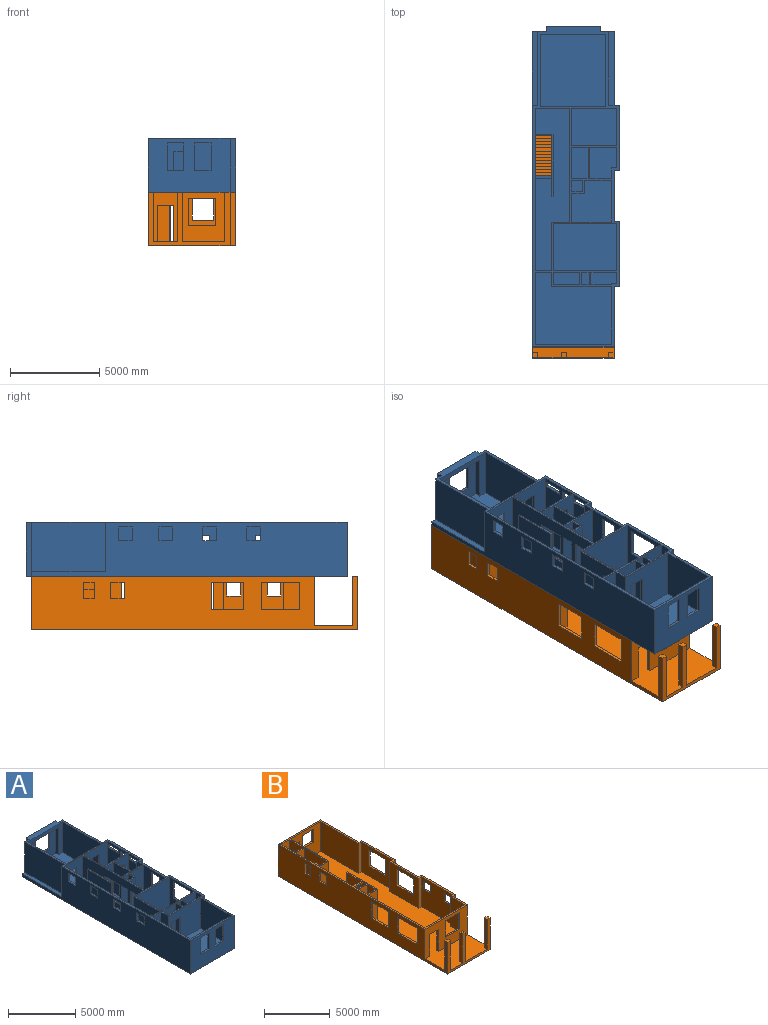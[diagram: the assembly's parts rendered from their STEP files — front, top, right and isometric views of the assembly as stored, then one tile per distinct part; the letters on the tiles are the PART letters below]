
ASSEMBLY  parts=2 mates=1
PART A: 174 faces, bbox 4876.8x17983.2x3025.8 mm
  f0: plane 17678.4x4572mm, normal (0,0,1), area 68948053.5mm2, adj f3,f4,f5,f7,f9,f10,f13,f15
  f1: plane 17983.2x4876.8mm, normal (0,0,-1), area 81833672.9mm2, adj f5,f6,f8,f11,f12,f14,f23,f24
  f2: plane 2565.4x101.6mm, normal (0,0,1), area 260644.6mm2, adj f4,f166,f167,f168
  f3: plane 1247.78x101.6mm, normal (0,-1,0), area 126773.9mm2, adj f0,f4,f166,f169
  f4: plane 3479.8x2771.78mm, normal (1,0,0), area 8251677mm2, adj f0,f2,f3,f167,f168,f169
  f5: plane 9118.6x3025.78mm, normal (1,0,0), area 23555975.7mm2, adj f0,f1,f49,f50,f58,f150,f151,f152
  f6: plane 17678.4x3025.78mm, normal (-1,0,0), area 39692581.9mm2, adj f1,f14,f22,f33,f36,f50,f150,f151
  f7: plane 2771.78x1143mm, normal (-1,0,0), area 2842978.2mm2, adj f0,f43,f50,f52,f141,f142,f143,f144
  f8: plane 3657.6x3025.78mm, normal (1,0,0), area 9371594.2mm2, adj f1,f26,f27,f50,f133,f134,f135,f136
  f9: plane 2771.78x2108.2mm, normal (-1,0,0), area 4473136.2mm2, adj f0,f42,f50,f53,f133,f134,f135,f136
  f10: plane 2771.78x2336.8mm, normal (-1,0,0), area 5362247.3mm2, adj f0,f50,f66,f78,f129,f130,f131,f132
  f11: plane 3025.78x2832.1mm, normal (1,0,0), area 7454460.9mm2, adj f1,f25,f26,f50,f129,f130,f131,f132
  f12: plane 3657.6x3025.78mm, normal (1,0,0), area 8279983.4mm2, adj f1,f24,f25,f50,f125,f126,f127,f128
  f13: plane 2771.78x2628.9mm, normal (-1,0,0), area 4499628.1mm2, adj f0,f16,f45,f50,f125,f126,f127,f128
  f14: plane 4572x3025.78mm, normal (0,-1,0), area 11046752.1mm2, adj f1,f6,f23,f50,f117,f118,f119,f120
  f15: plane 4267.2x2771.78mm, normal (0,1,0), area 9040627.1mm2, adj f0,f20,f48,f50,f117,f118,f119,f120
  f16: plane 3556x2771.78mm, normal (0,1,0), area 7946758.3mm2, adj f0,f13,f50,f65,f111,f112,f113
  f17: plane 3657.6x2771.78mm, normal (0,1,0), area 7144501.8mm2, adj f0,f18,f41,f50,f89,f90,f91,f92
  f18: plane 4038.6x2771.78mm, normal (1,0,0), area 11194090.5mm2, adj f0,f17,f37,f50
  f19: plane 2771.78x622.3mm, normal (-1,0,0), area 1724875.6mm2, adj f0,f46,f50,f64
  f20: plane 3238.5x2771.78mm, normal (-1,0,0), area 8976393.3mm2, adj f0,f15,f50,f61
  f21: plane 4140.2x304.8mm, normal (0,0,1), area 1261933mm2, adj f27,f28,f29,f34
  f22: plane 4140.2x304.8mm, normal (0,0,1), area 1261933mm2, adj f6,f33,f35,f36
  f23: plane 3390.9x3025.78mm, normal (1,0,0), area 10260100.4mm2, adj f1,f14,f24,f50
  f24: plane 3025.78x304.8mm, normal (0,-1,0), area 922256.2mm2, adj f1,f12,f23,f50
  f25: plane 3025.78x304.8mm, normal (0,1,0), area 922256.2mm2, adj f1,f11,f12,f50
  f26: plane 3025.78x304.8mm, normal (0,-1,0), area 922256.2mm2, adj f1,f8,f11,f50
  f27: plane 3025.78x609.6mm, normal (0,1,0), area 1767093.2mm2, adj f1,f8,f21,f28,f34,f50
  f28: plane 4140.2x254mm, normal (1,0,0), area 1051610.8mm2, adj f1,f21,f27,f29
  f29: plane 3025.78x762mm, normal (0,1,0), area 1460803.5mm2, adj f1,f21,f28,f30,f34,f50
  f30: plane 3025.78x304.8mm, normal (1,0,0), area 922256.2mm2, adj f1,f29,f31,f50
  f31: plane 3048x3025.78mm, normal (0,1,0), area 6899986.2mm2, adj f1,f30,f32,f50,f145,f146,f147,f148
  f32: plane 3025.78x304.8mm, normal (-1,0,0), area 922256.2mm2, adj f1,f31,f33,f50
  f33: plane 3025.78x762mm, normal (0,1,0), area 1460803.5mm2, adj f1,f6,f22,f32,f35,f50
  f34: plane 4140.2x2771.78mm, normal (1,0,0), area 11475702.9mm2, adj f21,f27,f29,f50
  f35: plane 4140.2x2771.78mm, normal (-1,0,0), area 11475702.9mm2, adj f22,f33,f36,f50
  f36: plane 2771.78x304.8mm, normal (0,1,0), area 844837mm2, adj f6,f22,f35,f50
  f37: plane 3657.6x2771.78mm, normal (0,-1,0), area 3370638.4mm2, adj f0,f18,f38,f40,f41,f50,f149
  f38: plane 2466.98x304.8mm, normal (1,0,0), area 751934mm2, adj f0,f37,f39,f149
  f39: plane 2743.2x2466.98mm, normal (0,-1,0), area 4444829.8mm2, adj f0,f38,f40,f145,f146,f147,f148,f149
  f40: plane 2466.98x304.8mm, normal (-1,0,0), area 751934mm2, adj f0,f37,f39,f149
  f41: plane 4038.6x2771.78mm, normal (-1,0,0), area 11194090.5mm2, adj f0,f17,f37,f50
  f42: plane 2771.78x2527.3mm, normal (0,-1,0), area 5559948.6mm2, adj f0,f9,f50,f54,f92,f93,f94
  f43: plane 2771.78x304.8mm, normal (0,1,0), area 844837mm2, adj f0,f7,f44,f50
  f44: plane 2771.78x596.9mm, normal (-1,0,0), area 1654472.5mm2, adj f0,f43,f50,f79
  f45: plane 3556x2771.78mm, normal (0,-1,0), area 9856431.9mm2, adj f0,f13,f50,f65
  f46: plane 2771.78x304.8mm, normal (0,1,0), area 844837mm2, adj f0,f19,f47,f50
  f47: plane 2771.78x50.8mm, normal (-1,0,0), area 140806.2mm2, adj f0,f46,f50,f62
  f48: plane 4013.2x2771.78mm, normal (1,0,0), area 11123687.4mm2, adj f0,f15,f50,f59
  f49: plane 2771.78x1943.1mm, normal (0,-1,0), area 3837452mm2, adj f0,f5,f50,f55,f89,f90,f91
  f50: plane 17983.2x4876.8mm, normal (0,0,1), area 11236106.6mm2, adj f5,f6,f7,f8,f9,f10,f11,f12
  f51: plane 2771.78x1739.9mm, normal (1,0,0), area 4822611.3mm2, adj f0,f50,f52,f79
  f52: plane 2771.78x1511.3mm, normal (0,-1,0), area 2743825.2mm2, adj f0,f7,f50,f51,f95,f96,f97
  f53: plane 2771.78x2527.3mm, normal (0,1,0), area 5559948.6mm2, adj f0,f9,f50,f54,f95,f96,f97
  f54: plane 2771.78x2108.2mm, normal (1,0,0), area 5843456.1mm2, adj f0,f42,f50,f53
  f55: plane 6388.1x2771.78mm, normal (-1,0,0), area 11925742.3mm2, adj f0,f49,f50,f56,f76,f82,f98,f99
  f56: plane 2771.78x1028.7mm, normal (0,1,0), area 2851324.9mm2, adj f0,f50,f55,f57
  f57: plane 2771.78x2730.5mm, normal (-1,0,0), area 6019947.6mm2, adj f0,f50,f56,f58,f108,f109,f110
  f58: plane 2771.78x914.4mm, normal (0,1,0), area 986127.1mm2, adj f0,f5,f50,f57,f105,f106,f107
  f59: plane 2771.78x914.4mm, normal (0,-1,0), area 986127.1mm2, adj f0,f48,f50,f60,f105,f106,f107
  f60: plane 2771.78x774.7mm, normal (-1,0,0), area 2147294.1mm2, adj f0,f50,f59,f61
  f61: plane 3352.8x2771.78mm, normal (0,-1,0), area 7357727.2mm2, adj f0,f20,f50,f60,f114,f115,f116
  f62: plane 2771.78x1143mm, normal (0,1,0), area 3168138.8mm2, adj f0,f47,f50,f63
  f63: plane 2771.78x673.1mm, normal (1,0,0), area 1865681.8mm2, adj f0,f50,f62,f64
  f64: plane 2771.78x1447.8mm, normal (0,-1,0), area 2103302.2mm2, adj f0,f19,f50,f63,f111,f112,f113
  f65: plane 2771.78x2628.9mm, normal (1,0,0), area 5738335.3mm2, adj f0,f16,f45,f50,f108,f109,f110
  f66: plane 2771.78x2222.5mm, normal (0,1,0), area 6160269.9mm2, adj f0,f10,f50,f67
  f67: plane 2771.78x1625.6mm, normal (1,0,0), area 3060639mm2, adj f0,f50,f66,f68,f101,f102,f103
  f68: plane 2771.78x711.2mm, normal (0,-1,0), area 1971286.4mm2, adj f0,f50,f67,f69
  f69: plane 2771.78x711.2mm, normal (1,0,0), area 1971286.4mm2, adj f0,f50,f68,f78
  f70: plane 2771.78x673.1mm, normal (1,0,0), area 1865681.8mm2, adj f0,f50,f74,f86
  f71: plane 2771.78x673.1mm, normal (1,0,0), area 1865681.8mm2, adj f50,f75,f84,f88
  f72: plane 739.78x609.6mm, normal (1,0,0), area 450966.8mm2, adj f50,f76,f82,f104
  f73: plane 2771.78x1739.9mm, normal (1,0,0), area 1725843.3mm2, adj f0,f50,f77,f80,f98,f99,f100
  f74: plane 2771.78x1460.5mm, normal (0,1,0), area 2112697.4mm2, adj f0,f50,f70,f87,f114,f115,f116
  f75: plane 2771.78x444.5mm, normal (0,1,0), area 1232054mm2, adj f50,f71,f85,f88
  f76: plane 2771.78x711.2mm, normal (0,1,0), area 1896125.2mm2, adj f0,f50,f55,f72,f83,f104
  f77: plane 2771.78x914.4mm, normal (0,1,0), area 2534511.1mm2, adj f0,f50,f73,f81
  f78: plane 2771.78x1511.3mm, normal (0,-1,0), area 4188983.6mm2, adj f0,f10,f50,f69
  f79: plane 2771.78x1206.5mm, normal (0,1,0), area 3344146.5mm2, adj f0,f44,f50,f51
  f80: plane 2771.78x914.4mm, normal (0,-1,0), area 2534511.1mm2, adj f0,f50,f73,f81
  f81: plane 2771.78x1739.9mm, normal (-1,0,0), area 4822611.3mm2, adj f0,f50,f77,f80
  f82: plane 2771.78x711.2mm, normal (0,-1,0), area 1896125.2mm2, adj f0,f50,f55,f72,f83,f104
  f83: plane 2771.78x609.6mm, normal (-1,0,0), area 1689674mm2, adj f0,f50,f76,f82
  f84: plane 2771.78x444.5mm, normal (0,-1,0), area 1232054mm2, adj f50,f71,f85,f88
  f85: plane 2771.78x673.1mm, normal (-1,0,0), area 1865681.8mm2, adj f50,f75,f84,f88
  f86: plane 2771.78x1460.5mm, normal (0,-1,0), area 4048177.4mm2, adj f0,f50,f70,f87
  f87: plane 2771.78x673.1mm, normal (-1,0,0), area 1865681.8mm2, adj f0,f50,f74,f86
  f88: plane 673.1x444.5mm, normal (0,0,1), area 299192.9mm2, adj f71,f75,f84,f85
  f89: plane 762x101.6mm, normal (0,0,-1), area 77419.2mm2, adj f17,f49,f90,f91
  f90: plane 2032x101.6mm, normal (-1,0,0), area 206451.2mm2, adj f0,f17,f49,f89
  f91: plane 2032x101.6mm, normal (1,0,0), area 206451.2mm2, adj f0,f17,f49,f89
  f92: plane 711.2x101.6mm, normal (0,0,-1), area 72257.9mm2, adj f17,f42,f93,f94
  f93: plane 2032x101.6mm, normal (-1,0,0), area 206451.2mm2, adj f0,f17,f42,f92
  f94: plane 2032x101.6mm, normal (1,0,0), area 206451.2mm2, adj f0,f17,f42,f92
  f95: plane 711.2x101.6mm, normal (0,0,-1), area 72257.9mm2, adj f52,f53,f96,f97
  f96: plane 2032x101.6mm, normal (1,0,0), area 206451.2mm2, adj f0,f52,f53,f95
  f97: plane 2032x101.6mm, normal (-1,0,0), area 206451.2mm2, adj f0,f52,f53,f95
  f98: plane 1524x101.6mm, normal (0,0,-1), area 154838.4mm2, adj f55,f73,f99,f100
  f99: plane 2032x101.6mm, normal (0,1,0), area 206451.2mm2, adj f0,f55,f73,f98
  f100: plane 2032x101.6mm, normal (0,-1,0), area 206451.2mm2, adj f0,f55,f73,f98
  f101: plane 711.2x101.6mm, normal (0,0,-1), area 72257.9mm2, adj f55,f67,f102,f103
  f102: plane 2032x101.6mm, normal (0,-1,0), area 206451.2mm2, adj f0,f55,f67,f101
  f103: plane 2032x101.6mm, normal (0,1,0), area 206451.2mm2, adj f0,f55,f67,f101
  f104: plane 609.6x101.6mm, normal (0,0,-1), area 61935.4mm2, adj f55,f72,f76,f82
  f105: plane 762x101.6mm, normal (0,0,-1), area 77419.2mm2, adj f58,f59,f106,f107
  f106: plane 2032x101.6mm, normal (1,0,0), area 206451.2mm2, adj f0,f58,f59,f105
  f107: plane 2032x101.6mm, normal (-1,0,0), area 206451.2mm2, adj f0,f58,f59,f105
  f108: plane 762x101.6mm, normal (0,0,-1), area 77419.2mm2, adj f57,f65,f109,f110
  f109: plane 2032x101.6mm, normal (0,-1,0), area 206451.2mm2, adj f0,f57,f65,f108
  f110: plane 2032x101.6mm, normal (0,1,0), area 206451.2mm2, adj f0,f57,f65,f108
  f111: plane 939.8x101.6mm, normal (0,0,-1), area 95483.7mm2, adj f16,f64,f112,f113
  f112: plane 2032x101.6mm, normal (1,0,0), area 206451.2mm2, adj f0,f16,f64,f111
  f113: plane 2032x101.6mm, normal (-1,0,0), area 206451.2mm2, adj f0,f16,f64,f111
  f114: plane 952.5x101.6mm, normal (0,0,-1), area 96774mm2, adj f61,f74,f115,f116
  f115: plane 2032x101.6mm, normal (-1,0,0), area 206451.2mm2, adj f0,f61,f74,f114
  f116: plane 2032x101.6mm, normal (1,0,0), area 206451.2mm2, adj f0,f61,f74,f114
  f117: plane 1524x152.4mm, normal (-1,0,0), area 232257.6mm2, adj f14,f15,f118,f119
  f118: plane 914.4x152.4mm, normal (0,0,1), area 139354.6mm2, adj f14,f15,f117,f120
  f119: plane 914.4x152.4mm, normal (0,0,-1), area 139354.6mm2, adj f14,f15,f117,f120
  f120: plane 1524x152.4mm, normal (1,0,0), area 232257.6mm2, adj f14,f15,f118,f119
  f121: plane 1524x152.4mm, normal (-1,0,0), area 232257.6mm2, adj f14,f15,f122,f123
  f122: plane 914.4x152.4mm, normal (0,0,1), area 139354.6mm2, adj f14,f15,f121,f124
  f123: plane 914.4x152.4mm, normal (0,0,-1), area 139354.6mm2, adj f14,f15,f121,f124
  f124: plane 1524x152.4mm, normal (1,0,0), area 232257.6mm2, adj f14,f15,f122,f123
  f125: plane 1524x152.4mm, normal (0,-1,0), area 232257.6mm2, adj f12,f13,f126,f127
  f126: plane 1828.8x152.4mm, normal (0,0,1), area 278709.1mm2, adj f12,f13,f125,f128
  f127: plane 1828.8x152.4mm, normal (0,0,-1), area 278709.1mm2, adj f12,f13,f125,f128
  f128: plane 1524x152.4mm, normal (0,1,0), area 232257.6mm2, adj f12,f13,f126,f127
  f129: plane 1219.2x152.4mm, normal (0,-1,0), area 185806.1mm2, adj f10,f11,f130,f131
  f130: plane 914.4x152.4mm, normal (0,0,1), area 139354.6mm2, adj f10,f11,f129,f132
  f131: plane 914.4x152.4mm, normal (0,0,-1), area 139354.6mm2, adj f10,f11,f129,f132
  f132: plane 1219.2x152.4mm, normal (0,1,0), area 185806.1mm2, adj f10,f11,f130,f131
  f133: plane 304.8x152.4mm, normal (0,-1,0), area 46451.5mm2, adj f8,f9,f134,f135
  f134: plane 1066.8x152.4mm, normal (0,0,1), area 162580.3mm2, adj f8,f9,f133,f136
  f135: plane 1066.8x152.4mm, normal (0,0,-1), area 162580.3mm2, adj f8,f9,f133,f136
  f136: plane 304.8x152.4mm, normal (0,1,0), area 46451.5mm2, adj f8,f9,f134,f135
  f137: plane 1371.6x152.4mm, normal (0,-1,0), area 209031.8mm2, adj f8,f9,f138,f139
  f138: plane 762x152.4mm, normal (0,0,1), area 116128.8mm2, adj f8,f9,f137,f140
  f139: plane 762x152.4mm, normal (0,0,-1), area 116128.8mm2, adj f8,f9,f137,f140
  f140: plane 1371.6x152.4mm, normal (0,1,0), area 209031.8mm2, adj f8,f9,f138,f139
  f141: plane 304.8x152.4mm, normal (0,-1,0), area 46451.5mm2, adj f7,f8,f142,f143
  f142: plane 1066.8x152.4mm, normal (0,0,1), area 162580.3mm2, adj f7,f8,f141,f144
  f143: plane 1066.8x152.4mm, normal (0,0,-1), area 162580.3mm2, adj f7,f8,f141,f144
  f144: plane 304.8x152.4mm, normal (0,1,0), area 46451.5mm2, adj f7,f8,f142,f143
  f145: plane 1524x152.4mm, normal (-1,0,0), area 232257.6mm2, adj f31,f39,f146,f148
  f146: plane 1524x152.4mm, normal (0,0,1), area 232257.6mm2, adj f31,f39,f145,f147
  f147: plane 1524x152.4mm, normal (1,0,0), area 232257.6mm2, adj f31,f39,f146,f148
  f148: plane 1524x152.4mm, normal (0,0,-1), area 232257.6mm2, adj f31,f39,f145,f147
  f149: plane 2743.2x304.8mm, normal (0,0,-1), area 836127.4mm2, adj f37,f38,f39,f40
  f150: plane 762x152.4mm, normal (0,1,0), area 116128.8mm2, adj f5,f6,f151,f152
  f151: plane 762x152.4mm, normal (0,0,1), area 116128.8mm2, adj f5,f6,f150,f153
  f152: plane 762x152.4mm, normal (0,0,-1), area 116128.8mm2, adj f5,f6,f150,f153
  f153: plane 762x152.4mm, normal (0,-1,0), area 116128.8mm2, adj f5,f6,f151,f152
  f154: plane 762x152.4mm, normal (0,1,0), area 116128.8mm2, adj f5,f6,f155,f156
  f155: plane 762x152.4mm, normal (0,0,1), area 116128.8mm2, adj f5,f6,f154,f157
  f156: plane 762x152.4mm, normal (0,0,-1), area 116128.8mm2, adj f5,f6,f154,f157
  f157: plane 762x152.4mm, normal (0,-1,0), area 116128.8mm2, adj f5,f6,f155,f156
  f158: plane 762x152.4mm, normal (0,1,0), area 116128.8mm2, adj f5,f6,f159,f160
  f159: plane 762x152.4mm, normal (0,0,1), area 116128.8mm2, adj f5,f6,f158,f161
  f160: plane 762x152.4mm, normal (0,0,-1), area 116128.8mm2, adj f5,f6,f158,f161
  f161: plane 762x152.4mm, normal (0,-1,0), area 116128.8mm2, adj f5,f6,f159,f160
  f162: plane 762x152.4mm, normal (0,1,0), area 116128.8mm2, adj f5,f6,f163,f164
  f163: plane 762x152.4mm, normal (0,0,1), area 116128.8mm2, adj f5,f6,f162,f165
  f164: plane 762x152.4mm, normal (0,0,-1), area 116128.8mm2, adj f5,f6,f162,f165
  f165: plane 762x152.4mm, normal (0,-1,0), area 116128.8mm2, adj f5,f6,f163,f164
  f166: plane 3479.8x3025.78mm, normal (-1,0,0), area 8855521.2mm2, adj f0,f1,f2,f3,f167,f168,f169,f170
  f167: plane 2771.78x101.6mm, normal (0,1,0), area 281612.3mm2, adj f0,f2,f4,f166
  f168: plane 1524x101.6mm, normal (0,-1,0), area 154838.4mm2, adj f2,f4,f166,f169
  f169: plane 914.4x101.6mm, normal (0,0,1), area 92903mm2, adj f3,f4,f166,f168
  f170: plane 939.8x254mm, normal (0,-1,0), area 238709.2mm2, adj f0,f1,f5,f166
  f171: plane 939.8x127mm, normal (0,1,0), area 119354.6mm2, adj f0,f5,f166,f172
  f172: plane 939.8x177.8mm, normal (0,0,1), area 167096.4mm2, adj f5,f166,f171,f173
  f173: plane 939.8x127mm, normal (0,1,0), area 119354.6mm2, adj f1,f5,f166,f172
PART B: 161 faces, bbox 4876.8x18288x2975 mm
  f0: plane 2771.78x965.2mm, normal (1,0,0), area 2396312.3mm2, adj f1,f2,f35,f59,f153,f154
  f1: plane 18288x4724.4mm, normal (0,0,1), area 76402427.8mm2, adj f0,f4,f5,f6,f7,f9,f10,f11
  f2: plane 914.4x652.48mm, normal (0,-0.73,-0.69), area 820247.4mm2, adj f0,f4,f153,f154
  f3: plane 1847.85x1609.16mm, normal (-1,0,0), area 1519878.4mm2, adj f35,f58,f133,f134,f135,f136,f137,f138
  f4: plane 2771.78x965.2mm, normal (-1,0,0), area 1157605.1mm2, adj f1,f2,f35,f59,f111,f112,f113,f153
  f5: plane 3641.16x2771.78mm, normal (1,0,0), area 6003944.3mm2, adj f1,f35,f47,f99,f100,f101,f102,f124
  f6: plane 18288x2974.98mm, normal (-1,0,0), area 41199595mm2, adj f1,f7,f17,f23,f28,f29,f34,f35
  f7: plane 4572x2974.98mm, normal (0,1,0), area 10257076.3mm2, adj f1,f6,f16,f23,f35,f88,f89,f90
  f8: plane 3657.6x2974.98mm, normal (1,0,0), area 9719980.6mm2, adj f19,f20,f23,f35,f72,f73,f74,f75
  f9: plane 3352.8x2771.78mm, normal (-1,0,0), area 8131919.2mm2, adj f1,f35,f36,f46,f72,f73,f74,f75
  f10: plane 6146.8x2771.78mm, normal (1,0,0), area 10998849mm2, adj f1,f35,f44,f56,f103,f104,f105,f106
  f11: plane 2771.78x901.7mm, normal (1,0,0), area 2499309.5mm2, adj f1,f35,f55,f60
  f12: plane 2771.78x914.4mm, normal (0,-1,0), area 2534511.1mm2, adj f1,f35,f43,f49
  f13: plane 2771.78x2425.7mm, normal (1,0,0), area 6166076.4mm2, adj f1,f35,f51,f53,f95,f96,f97,f98
  f14: plane 3657.6x2974.98mm, normal (1,0,0), area 8094177.4mm2, adj f15,f22,f23,f35,f84,f85,f86,f87
  f15: plane 2974.98x304.8mm, normal (0,1,0), area 906772.4mm2, adj f14,f16,f23,f35
  f16: plane 4140.2x2974.98mm, normal (1,0,0), area 12316991.5mm2, adj f7,f15,f23,f35
  f17: plane 4572x2974.98mm, normal (0,-1,0), area 3463541.5mm2, adj f1,f6,f18,f23,f25,f26,f27,f29
  f18: plane 4000.5x2974.98mm, normal (1,0,0), area 5987528.3mm2, adj f1,f17,f19,f23,f24,f26,f34,f35
  f19: plane 2974.98x304.8mm, normal (0,-1,0), area 906772.4mm2, adj f8,f18,f23,f35
  f20: plane 2974.98x304.8mm, normal (0,1,0), area 906772.4mm2, adj f8,f21,f23,f35
  f21: plane 2974.98x2832.1mm, normal (1,0,0), area 5638335.5mm2, adj f20,f22,f23,f35,f80,f81,f82,f83
  f22: plane 2974.98x304.8mm, normal (0,-1,0), area 906772.4mm2, adj f14,f21,f23,f35
  f23: plane 18288x4876.8mm, normal (0,0,-1), area 85416603.4mm2, adj f6,f7,f8,f14,f15,f16,f17,f18
  f24: plane 2771.78x304.8mm, normal (0,1,0), area 844837mm2, adj f1,f18,f25,f26
  f25: plane 2771.78x304.8mm, normal (-1,0,0), area 844837mm2, adj f1,f17,f24,f26
  f26: plane 304.8x304.8mm, normal (0,0,1), area 92903mm2, adj f17,f18,f24,f25
  f27: plane 2771.78x304.8mm, normal (1,0,0), area 844837mm2, adj f1,f17,f28,f29
  f28: plane 2771.78x304.8mm, normal (0,1,0), area 844837mm2, adj f1,f6,f27,f29
  f29: plane 304.8x304.8mm, normal (0,0,1), area 92903mm2, adj f6,f17,f27,f28
  f30: plane 2771.78x304.8mm, normal (1,0,0), area 844837mm2, adj f1,f17,f31,f33
  f31: plane 2771.78x304.8mm, normal (0,1,0), area 844837mm2, adj f1,f30,f32,f33
  f32: plane 2771.78x304.8mm, normal (-1,0,0), area 844837mm2, adj f1,f17,f31,f33
  f33: plane 304.8x304.8mm, normal (0,0,1), area 92903mm2, adj f17,f30,f31,f32
  f34: plane 4572x2771.78mm, normal (0,-1,0), area 8491918.5mm2, adj f1,f6,f18,f35,f65,f66,f67,f68
  f35: plane 15849.6x4876.8mm, normal (0,0,1), area 7597252.4mm2, adj f0,f3,f4,f5,f6,f7,f8,f9
  f36: plane 2771.78x304.8mm, normal (0,-1,0), area 844837mm2, adj f1,f9,f35,f37
  f37: plane 3136.9x2771.78mm, normal (-1,0,0), area 5907689.8mm2, adj f1,f35,f36,f38,f80,f81,f82,f83
  f38: plane 2771.78x304.8mm, normal (0,1,0), area 844837mm2, adj f1,f35,f37,f39
  f39: plane 3352.8x2771.78mm, normal (-1,0,0), area 6506116mm2, adj f1,f35,f38,f40,f84,f85,f86,f87
  f40: plane 2771.78x304.8mm, normal (0,-1,0), area 844837mm2, adj f1,f35,f39,f41
  f41: plane 4140.2x2771.78mm, normal (-1,0,0), area 11475702.9mm2, adj f1,f35,f40,f42
  f42: plane 3251.2x2771.78mm, normal (0,-1,0), area 5667085.4mm2, adj f1,f35,f41,f48,f88,f89,f90,f91
  f43: plane 2771.78x1498.6mm, normal (1,0,0), area 4153782mm2, adj f1,f12,f35,f50
  f44: plane 4267.2x2771.78mm, normal (0,1,0), area 7647081.5mm2, adj f1,f10,f35,f45,f65,f66,f67,f68
  f45: plane 2771.78x1562.1mm, normal (-1,0,0), area 4329789.7mm2, adj f1,f35,f44,f46
  f46: plane 2771.78x304.8mm, normal (0,1,0), area 844837mm2, adj f1,f9,f35,f45
  f47: plane 2771.78x1016mm, normal (0,-1,0), area 2816123.4mm2, adj f1,f5,f35,f48
  f48: plane 4127.5x2771.78mm, normal (1,0,0), area 8756635.7mm2, adj f1,f35,f42,f47,f117,f118,f119,f120
  f49: plane 2771.78x1498.6mm, normal (-1,0,0), area 2915074.8mm2, adj f1,f12,f35,f50,f120,f121,f122
  f50: plane 2771.78x914.4mm, normal (0,1,0), area 2534511.1mm2, adj f1,f35,f43,f49
  f51: plane 2771.78x914.4mm, normal (0,-1,0), area 2534511.1mm2, adj f1,f13,f35,f52
  f52: plane 2771.78x2425.7mm, normal (-1,0,0), area 5278336.2mm2, adj f1,f35,f51,f53,f117,f118,f119
  f53: plane 2771.78x914.4mm, normal (0,1,0), area 2534511.1mm2, adj f1,f13,f35,f52
  f54: plane 2771.78x901.7mm, normal (-1,0,0), area 1260602.3mm2, adj f1,f35,f55,f60,f114,f115,f116
  f55: plane 2771.78x914.4mm, normal (0,1,0), area 2534511.1mm2, adj f1,f11,f35,f54
  f56: plane 2771.78x1016mm, normal (0,-1,0), area 2816123.4mm2, adj f1,f10,f35,f57
  f57: plane 3238.5x2771.78mm, normal (1,0,0), area 6498978.9mm2, adj f1,f35,f56,f58,f111,f112,f113,f114
  f58: plane 2771.78x101.6mm, normal (0,1,0), area 281612.3mm2, adj f1,f3,f35,f57,f123
  f59: plane 2771.78x914.4mm, normal (0,1,0), area 2534511.1mm2, adj f0,f1,f4,f35
  f60: plane 2771.78x914.4mm, normal (0,-1,0), area 2534511.1mm2, adj f1,f11,f35,f54
  f61: plane 558.8x203.2mm, normal (0,1,0), area 113548.2mm2, adj f1,f23,f62,f64
  f62: plane 762x203.2mm, normal (-1,0,0), area 154838.4mm2, adj f1,f23,f61,f63
  f63: plane 558.8x203.2mm, normal (0,-1,0), area 113548.2mm2, adj f1,f23,f62,f64
  f64: plane 762x203.2mm, normal (1,0,0), area 154838.4mm2, adj f1,f23,f61,f63
  f65: plane 914.4x152.4mm, normal (0,0,-1), area 139354.6mm2, adj f34,f44,f66,f67
  f66: plane 2032x152.4mm, normal (1,0,0), area 309676.8mm2, adj f1,f34,f44,f65
  f67: plane 2032x152.4mm, normal (-1,0,0), area 309676.8mm2, adj f1,f34,f44,f65
  f68: plane 1524x152.4mm, normal (0,0,1), area 232257.6mm2, adj f34,f44,f69,f71
  f69: plane 1524x152.4mm, normal (1,0,0), area 232257.6mm2, adj f34,f44,f68,f70
  f70: plane 1524x152.4mm, normal (0,0,-1), area 232257.6mm2, adj f34,f44,f69,f71
  f71: plane 1524x152.4mm, normal (-1,0,0), area 232257.6mm2, adj f34,f44,f68,f70
  f72: plane 762x152.4mm, normal (0,0,1), area 116128.8mm2, adj f8,f9,f73,f75
  f73: plane 762x152.4mm, normal (0,-1,0), area 116128.8mm2, adj f8,f9,f72,f74
  f74: plane 762x152.4mm, normal (0,0,-1), area 116128.8mm2, adj f8,f9,f73,f75
  f75: plane 762x152.4mm, normal (0,1,0), area 116128.8mm2, adj f8,f9,f72,f74
  f76: plane 762x152.4mm, normal (0,0,1), area 116128.8mm2, adj f8,f9,f77,f78
  f77: plane 762x152.4mm, normal (0,1,0), area 116128.8mm2, adj f8,f9,f76,f79
  f78: plane 762x152.4mm, normal (0,-1,0), area 116128.8mm2, adj f8,f9,f76,f79
  f79: plane 762x152.4mm, normal (0,0,-1), area 116128.8mm2, adj f8,f9,f77,f78
  f80: plane 1828.8x152.4mm, normal (0,0,1), area 278709.1mm2, adj f21,f37,f81,f83
  f81: plane 1524x152.4mm, normal (0,-1,0), area 232257.6mm2, adj f21,f37,f80,f82
  f82: plane 1828.8x152.4mm, normal (0,0,-1), area 278709.1mm2, adj f21,f37,f81,f83
  f83: plane 1524x152.4mm, normal (0,1,0), area 232257.6mm2, adj f21,f37,f80,f82
  f84: plane 1828.8x152.4mm, normal (0,0,1), area 278709.1mm2, adj f14,f39,f85,f87
  f85: plane 1524x152.4mm, normal (0,-1,0), area 232257.6mm2, adj f14,f39,f84,f86
  f86: plane 1828.8x152.4mm, normal (0,0,-1), area 278709.1mm2, adj f14,f39,f85,f87
  f87: plane 1524x152.4mm, normal (0,1,0), area 232257.6mm2, adj f14,f39,f84,f86
  f88: plane 1219.2x152.4mm, normal (0,0,1), area 185806.1mm2, adj f7,f42,f89,f91
  f89: plane 1219.2x152.4mm, normal (1,0,0), area 185806.1mm2, adj f7,f42,f88,f90
  f90: plane 1219.2x152.4mm, normal (0,0,-1), area 185806.1mm2, adj f7,f42,f89,f91
  f91: plane 1219.2x152.4mm, normal (-1,0,0), area 185806.1mm2, adj f7,f42,f88,f90
  f92: plane 2032x152.4mm, normal (1,0,0), area 309676.8mm2, adj f1,f7,f42,f93
  f93: plane 914.4x152.4mm, normal (0,0,-1), area 139354.6mm2, adj f7,f42,f92,f94
  f94: plane 2032x152.4mm, normal (-1,0,0), area 309676.8mm2, adj f1,f7,f42,f93
  f95: plane 609.6x152.4mm, normal (0,0,1), area 92903mm2, adj f6,f13,f96,f98
  f96: plane 914.4x152.4mm, normal (0,1,0), area 139354.6mm2, adj f6,f13,f95,f97
  f97: plane 609.6x152.4mm, normal (0,0,-1), area 92903mm2, adj f6,f13,f96,f98
  f98: plane 914.4x152.4mm, normal (0,-1,0), area 139354.6mm2, adj f6,f13,f95,f97
  f99: plane 762x152.4mm, normal (0,0,1), area 116128.8mm2, adj f5,f6,f100,f102
  f100: plane 914.4x152.4mm, normal (0,1,0), area 139354.6mm2, adj f5,f6,f99,f101
  f101: plane 762x152.4mm, normal (0,0,-1), area 116128.8mm2, adj f5,f6,f100,f102
  f102: plane 914.4x152.4mm, normal (0,-1,0), area 139354.6mm2, adj f5,f6,f99,f101
  f103: plane 1828.8x152.4mm, normal (0,0,1), area 278709.1mm2, adj f6,f10,f104,f106
  f104: plane 1524x152.4mm, normal (0,1,0), area 232257.6mm2, adj f6,f10,f103,f105
  f105: plane 1828.8x152.4mm, normal (0,0,-1), area 278709.1mm2, adj f6,f10,f104,f106
  f106: plane 1524x152.4mm, normal (0,-1,0), area 232257.6mm2, adj f6,f10,f103,f105
  f107: plane 2133.6x152.4mm, normal (0,0,1), area 325160.6mm2, adj f6,f10,f108,f110
  f108: plane 1524x152.4mm, normal (0,1,0), area 232257.6mm2, adj f6,f10,f107,f109
  f109: plane 2133.6x152.4mm, normal (0,0,-1), area 325160.6mm2, adj f6,f10,f108,f110
  f110: plane 1524x152.4mm, normal (0,-1,0), area 232257.6mm2, adj f6,f10,f107,f109
  f111: plane 609.6x101.6mm, normal (0,0,-1), area 61935.4mm2, adj f4,f57,f112,f113
  f112: plane 2032x101.6mm, normal (0,1,0), area 206451.2mm2, adj f1,f4,f57,f111
  f113: plane 2032x101.6mm, normal (0,-1,0), area 206451.2mm2, adj f1,f4,f57,f111
  f114: plane 609.6x101.6mm, normal (0,0,-1), area 61935.4mm2, adj f54,f57,f115,f116
  f115: plane 2032x101.6mm, normal (0,1,0), area 206451.2mm2, adj f1,f54,f57,f114
  f116: plane 2032x101.6mm, normal (0,-1,0), area 206451.2mm2, adj f1,f54,f57,f114
  f117: plane 711.2x101.6mm, normal (0,0,-1), area 72257.9mm2, adj f48,f52,f118,f119
  f118: plane 2032x101.6mm, normal (0,1,0), area 206451.2mm2, adj f1,f48,f52,f117
  f119: plane 2032x101.6mm, normal (0,-1,0), area 206451.2mm2, adj f1,f48,f52,f117
  f120: plane 609.6x101.6mm, normal (0,0,-1), area 61935.4mm2, adj f48,f49,f121,f122
  f121: plane 2032x101.6mm, normal (0,1,0), area 206451.2mm2, adj f1,f48,f49,f120
  f122: plane 2032x101.6mm, normal (0,-1,0), area 206451.2mm2, adj f1,f48,f49,f120
  f123: plane 923.93x838.2mm, normal (1,0,0), area 451408mm2, adj f1,f58,f124,f125,f126,f127,f128,f129
  f124: plane 914.4x184.79mm, normal (0,1,0), area 168967.4mm2, adj f1,f5,f123,f125
  f125: plane 914.4x174.81mm, normal (0,0,1), area 159847.9mm2, adj f5,f123,f124,f126
  f126: plane 914.4x184.79mm, normal (0,1,0), area 168967.4mm2, adj f5,f123,f125,f127
  f127: plane 914.4x174.81mm, normal (0,0,1), area 159847.9mm2, adj f5,f123,f126,f128
  f128: plane 914.4x184.79mm, normal (0,1,0), area 168967.4mm2, adj f5,f123,f127,f129
  f129: plane 914.4x174.81mm, normal (0,0,1), area 159847.9mm2, adj f5,f123,f128,f130
  f130: plane 914.4x184.79mm, normal (0,1,0), area 168967.4mm2, adj f5,f123,f129,f131
  f131: plane 914.4x174.81mm, normal (0,0,1), area 159847.9mm2, adj f5,f123,f130,f132
  f132: plane 914.4x184.79mm, normal (0,1,0), area 168967.4mm2, adj f5,f123,f131,f133
  f133: plane 914.4x174.81mm, normal (0,0,1), area 159847.9mm2, adj f3,f5,f123,f132,f134
  f134: plane 914.4x184.79mm, normal (0,1,0), area 168967.4mm2, adj f3,f5,f133,f135
  f135: plane 914.4x174.81mm, normal (0,0,1), area 159847.9mm2, adj f3,f5,f134,f136
  f136: plane 914.4x184.79mm, normal (0,1,0), area 168967.4mm2, adj f3,f5,f135,f137
  f137: plane 914.4x174.81mm, normal (0,0,1), area 159847.9mm2, adj f3,f5,f136,f138
  f138: plane 914.4x184.79mm, normal (0,1,0), area 168967.4mm2, adj f3,f5,f137,f139
  f139: plane 914.4x174.81mm, normal (0,0,1), area 159847.9mm2, adj f3,f5,f138,f140
  f140: plane 914.4x184.79mm, normal (0,1,0), area 168967.4mm2, adj f3,f5,f139,f141
  f141: plane 914.4x174.81mm, normal (0,0,1), area 159847.9mm2, adj f3,f5,f140,f142
  f142: plane 914.4x184.79mm, normal (0,1,0), area 168967.4mm2, adj f3,f5,f141,f143
  f143: plane 914.4x174.81mm, normal (0,0,1), area 159847.9mm2, adj f3,f5,f142,f144
  f144: plane 914.4x184.79mm, normal (0,1,0), area 168967.4mm2, adj f3,f5,f143,f145
  f145: plane 914.4x174.81mm, normal (0,0,1), area 159847.9mm2, adj f3,f5,f144,f146
  f146: plane 914.4x184.79mm, normal (0,1,0), area 168967.4mm2, adj f3,f5,f145,f147
  f147: plane 914.4x174.81mm, normal (0,0,1), area 159847.9mm2, adj f3,f5,f146,f148
  f148: plane 914.4x184.79mm, normal (0,1,0), area 168967.4mm2, adj f3,f5,f147,f149
  f149: plane 914.4x174.81mm, normal (0,0,1), area 159847.9mm2, adj f3,f5,f148,f150
  f150: plane 914.4x184.79mm, normal (0,1,0), area 168967.4mm2, adj f3,f5,f149,f151
  f151: plane 914.4x174.81mm, normal (0,0,1), area 159847.9mm2, adj f3,f5,f150,f152
  f152: plane 914.4x184.79mm, normal (0,1,0), area 168967.4mm2, adj f3,f5,f35,f151
  f153: plane 914.4x127mm, normal (0,-1,0), area 116128.8mm2, adj f0,f2,f4,f35
  f154: plane 1992.29x914.4mm, normal (0,-1,0), area 1821751.4mm2, adj f0,f1,f2,f4
  f155: plane 1884.6x914.4mm, normal (0,1,0), area 1723278.4mm2, adj f157,f158,f159,f160
  f156: plane 1076.91x914.4mm, normal (0,-1,0), area 984730.5mm2, adj f157,f158,f159,f160
  f157: plane 914.4x807.69mm, normal (0,-0.73,-0.69), area 1015354.8mm2, adj f155,f156,f158,f160
  f158: plane 1884.6x762mm, normal (-1,0,0), area 1128337mm2, adj f155,f156,f157,f159
  f159: plane 914.4x762mm, normal (0,0,1), area 696772.8mm2, adj f155,f156,f158,f160
  f160: plane 1884.6x762mm, normal (1,0,0), area 1128337mm2, adj f155,f156,f157,f159
PLACE A t=(1526.54,-3743.67,5493.85)mm
PLACE B t=(1526.54,-4353.27,2264.87)mm
MATE fastened A.f1 <-> B.f35  axis (0,0,1) through (6403.34,-352.77,5239.85)mm
